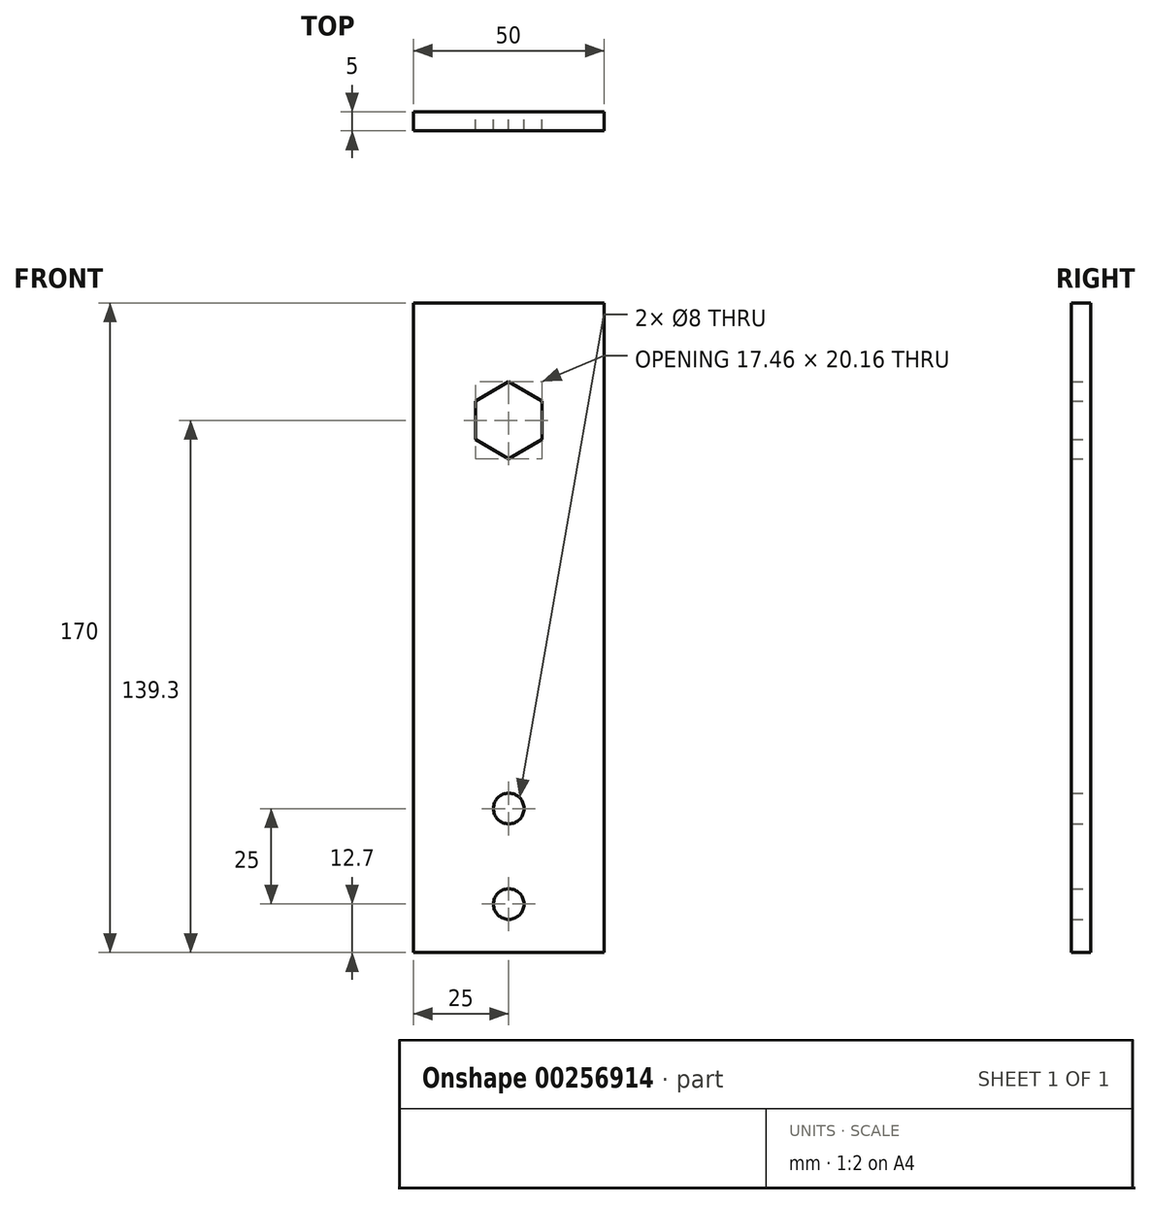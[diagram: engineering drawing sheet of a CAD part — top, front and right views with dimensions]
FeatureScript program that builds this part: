
annotation { "Feature Type Name" : "Feature", "Feature Type Description" : "" }
export const myFeature = defineFeature(function(context is Context, id is Id, definition is map)
    precondition{}
    {
        {
            var Q0;
            Q0=qCreatedBy(makeId("Front.planeOp"),FACE);
            var sketch = newSketch(context, id + "F0", { "sketchPlane" : qUnion([Q0])});
            skLineSegment(sketch, "E0.bottom", {"start": v(0, 0) * mm, "end": v(50, 0) * mm});
            skLineSegment(sketch, "E0.top", {"start": v(0, 170) * mm, "end": v(50, 170) * mm});
            skLineSegment(sketch, "E0.left", {"start": v(0, 0) * mm, "end": v(0, 170) * mm});
            skLineSegment(sketch, "E0.right", {"start": v(50, 0) * mm, "end": v(50, 170) * mm});
            skCircle(sketch, "E1", {"center": v(25, 12.7) * mm, "radius": 4 * mm});
            skPoint(sketch, "E1.centerSnap0", {"position": v(25, 0) * mm});
            skCircle(sketch, "E2", {"center": v(25, 37.7) * mm, "radius": 4 * mm});
            skCircle(sketch, "E3.cCircle", {"center": v(25, 139.3) * mm, "radius": 8.73 * mm, "construction": true});
            skLineSegment(sketch, "E3.0", {"start": v(33.73, 144.34) * mm, "end": v(33.73, 134.26) * mm});
            skLineSegment(sketch, "E3.1", {"start": v(33.73, 134.26) * mm, "end": v(25, 129.22) * mm});
            skLineSegment(sketch, "E3.2", {"start": v(25, 129.22) * mm, "end": v(16.27, 134.26) * mm});
            skLineSegment(sketch, "E3.3", {"start": v(16.27, 134.26) * mm, "end": v(16.27, 144.34) * mm});
            skLineSegment(sketch, "E3.4", {"start": v(16.27, 144.34) * mm, "end": v(25, 149.38) * mm});
            skLineSegment(sketch, "E3.5", {"start": v(25, 149.38) * mm, "end": v(33.73, 144.34) * mm});
            skPoint(sketch, "E3.0.midPoint", {"position": v(33.73, 139.3) * mm});
            skSolve(sketch);
        }
        {
            var Q0;
            Q0=makeQuery(id+"F0.imprint","IMPRINT",FACE,{"disambiguationData":[TD([[makeQuery(id+"F0.imprint","IMPRINT",EDGE,{"derivedFrom":sQuery(id+"F0.wireOp",EDGE,"E0.bottom")}),1.0]])]});
            extrude(context, id + "F1", {"entities" : qUnion([Q0]), "depth" : 5 * mm});
        }
    });
